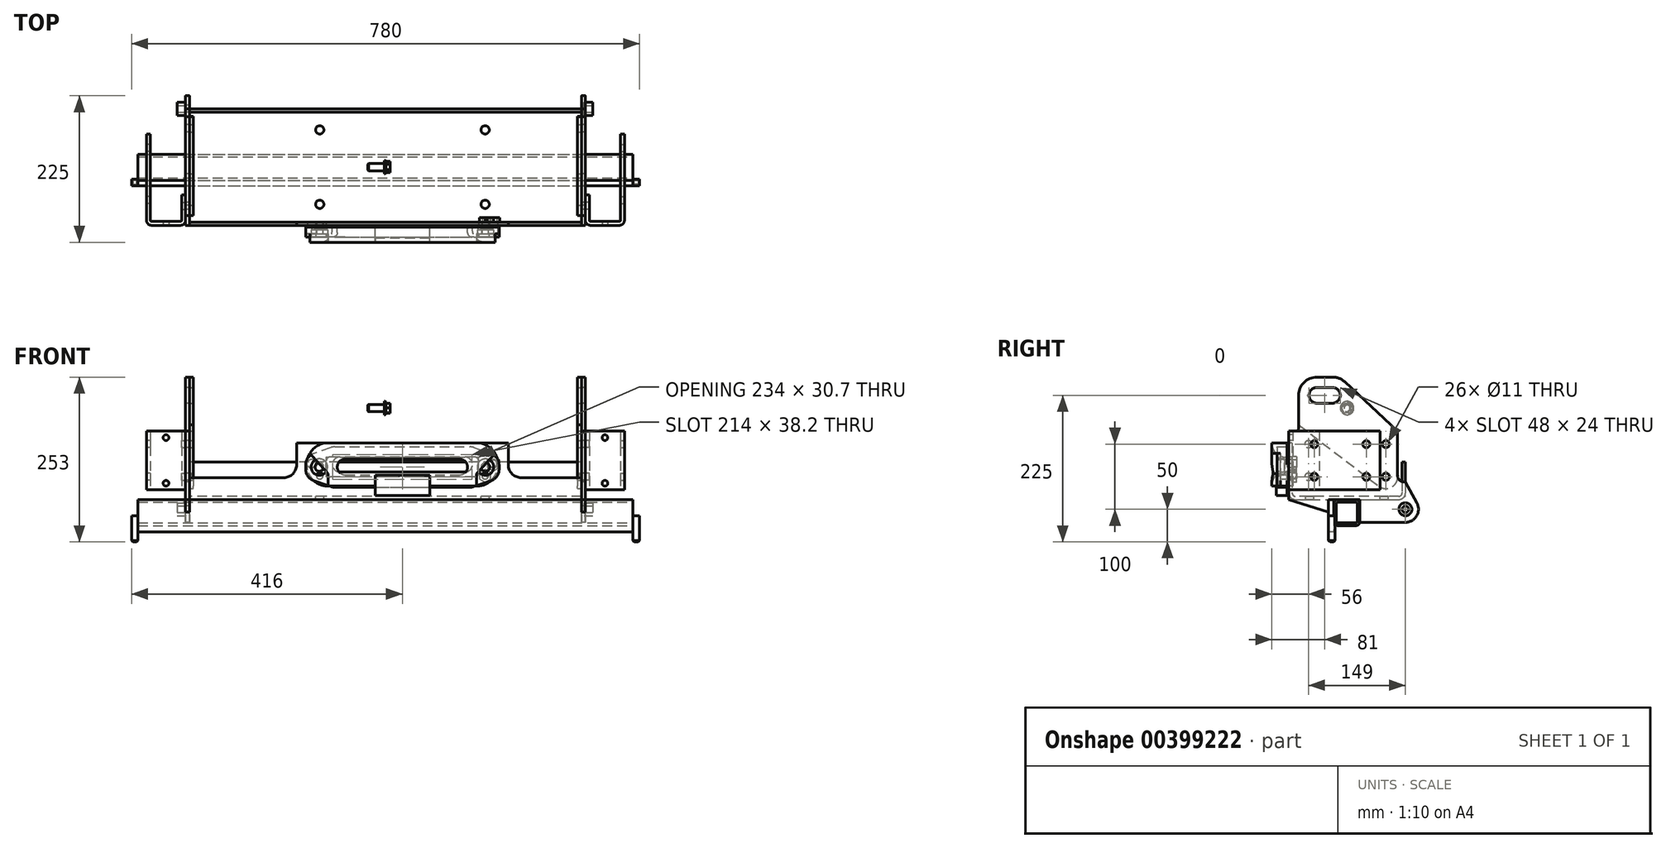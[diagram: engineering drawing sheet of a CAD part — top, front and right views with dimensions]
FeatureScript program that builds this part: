
annotation { "Feature Type Name" : "Feature", "Feature Type Description" : "" }
export const myFeature = defineFeature(function(context is Context, id is Id, definition is map)
    precondition{}
    {
        {
            var Q0;
            Q0=qCreatedBy(makeId("Right.planeOp"),FACE);
            var sketch = newSketch(context, id + "F0", { "sketchPlane" : qUnion([Q0])});
            skLineSegment(sketch, "E0", {"start": v(-84.5, 0) * mm, "end": v(84.5, 0) * mm});
            skLineSegment(sketch, "E1", {"start": v(-84.5, 0) * mm, "end": v(-84.5, 81.8) * mm});
            skLineSegment(sketch, "E2", {"start": v(84.5, 0) * mm, "end": v(84.5, 52.5) * mm});
            skLineSegment(sketch, "E3.0", {"start": v(-89.5, -5) * mm, "end": v(-89.5, 81.8) * mm});
            skLineSegment(sketch, "E3.1", {"start": v(-89.5, -5) * mm, "end": v(89.5, -5) * mm});
            skLineSegment(sketch, "E3.2", {"start": v(89.5, -5) * mm, "end": v(89.5, 52.5) * mm});
            skLineSegment(sketch, "E4", {"start": v(-89.5, 81.8) * mm, "end": v(-84.5, 81.8) * mm});
            skLineSegment(sketch, "E5", {"start": v(84.5, 52.5) * mm, "end": v(89.5, 52.5) * mm});
            skSolve(sketch);
        }
        {
            var Q0;
            Q0=qSketchRegion(id+"F0",true);
            extrude(context, id + "F1", {"entities" : qUnion([Q0]), "endBound" : BoundingType.SYMMETRIC, "depth" : 896 * mm});
        }
        {
            var Q0;
            Q0=makeQuery(id+"F1.opExtrude","SWEPT_FACE",FACE,{"disambiguationData":[OSD([sQuery(id+"F0.wireOp",EDGE,"E3.0")])]});
            var sketch = newSketch(context, id + "F2", { "sketchPlane" : qUnion([Q0])});
            skLineSegment(sketch, "E6", {"start": v(-448, 28.5) * mm, "end": v(-162.5, 28.5) * mm});
            skLineSegment(sketch, "E7", {"start": v(-162.5, 28.5) * mm, "end": v(-162.5, 81.8) * mm});
            skLineSegment(sketch, "E8", {"start": v(-162.5, 81.8) * mm, "end": v(162.5, 81.8) * mm});
            skLineSegment(sketch, "E9", {"start": v(162.5, 81.8) * mm, "end": v(162.5, 28.5) * mm});
            skLineSegment(sketch, "E10", {"start": v(162.5, 28.5) * mm, "end": v(448, 28.5) * mm});
            skLineSegment(sketch, "E11.bottom", {"start": v(-117, 60.2) * mm, "end": v(117, 60.2) * mm});
            skLineSegment(sketch, "E11.top", {"start": v(-117, 29.5) * mm, "end": v(117, 29.5) * mm});
            skLineSegment(sketch, "E11.left", {"start": v(-117, 60.2) * mm, "end": v(-117, 29.5) * mm});
            skLineSegment(sketch, "E11.right", {"start": v(117, 60.2) * mm, "end": v(117, 29.5) * mm});
            skCircle(sketch, "E12", {"center": v(-139.7, 50.1) * mm, "radius": 6.35 * mm});
            skCircle(sketch, "E13", {"center": v(139.7, 50.1) * mm, "radius": 6.35 * mm});
            skCircle(sketch, "E14", {"center": v(-127, 31.5) * mm, "radius": 5.1 * mm});
            skCircle(sketch, "E15", {"center": v(127, 31.5) * mm, "radius": 5.1 * mm});
            skLineSegment(sketch, "E16", {"start": v(-139.7, 50.1) * mm, "end": v(139.7, 50.1) * mm, "construction": true});
            skLineSegment(sketch, "E17", {"start": v(0, 60.2) * mm, "end": v(0, 29.5) * mm, "construction": true});
            skCircle(sketch, "E18", {"center": v(-127.5, 44.85) * mm, "radius": 5.1 * mm});
            skCircle(sketch, "E19.MirrorC", {"center": v(127.5, 44.85) * mm, "radius": 5.1 * mm});
            skLineSegment(sketch, "E20", {"start": v(-117, 44.85) * mm, "end": v(117, 44.85) * mm, "construction": true});
            skLineSegment(sketch, "E21", {"start": v(-117, 44.85) * mm, "end": v(-162.5, 44.85) * mm, "construction": true});
            skCircle(sketch, "E22", {"center": v(-127.5, 44.85) * mm, "radius": 6 * mm, "construction": true});
            skCircle(sketch, "E23", {"center": v(-139.7, 50.1) * mm, "radius": 6 * mm, "construction": true});
            skLineSegment(sketch, "E24", {"start": v(-127.5, 44.85) * mm, "end": v(-127.5, 24.22) * mm, "construction": true});
            skSolve(sketch);
        }
        {
            var Q0;
            Q0=qSketchRegion(id+"F2",true);
            var Q1;
            {var subQ0=sQuery(id+"F2.wireOp",EDGE,"E6");Q1=makeQuery(id+"F2.imprint","IMPRINT",FACE,{"disambiguationData":[TD([[makeQuery(id+"F2.imprint","IMPRINT",EDGE,{"derivedFrom":subQ0}),1.0]])]});}
            var Q2;
            {var subQ0=sQuery(id+"F2.wireOp",EDGE,"E9");Q2=makeQuery(id+"F2.imprint","IMPRINT",FACE,{"disambiguationData":[TD([[makeQuery(id+"F2.imprint","IMPRINT",EDGE,{"derivedFrom":subQ0}),1.0]])]});}
            extrude(context, id + "F3", {"entities" : qUnion([Q0, Q1, Q2]), "operationType" : NewBodyOperationType.REMOVE, "endBound" : BoundingType.UP_TO_NEXT, "oppositeDirection" : true, "depth" : 25 * mm});
        }
        {
            var Q0;
            Q0=makeQuery(id+"F1.opExtrude","SWEPT_FACE",FACE,{"disambiguationData":[OSD([sQuery(id+"F0.wireOp",EDGE,"E0")])]});
            var sketch = newSketch(context, id + "F4", { "sketchPlane" : qUnion([Q0])});
            skLineSegment(sketch, "E25.bottom", {"start": v(-127, 57.15) * mm, "end": v(127, 57.15) * mm, "construction": true});
            skLineSegment(sketch, "E25.top", {"start": v(-127, -57.15) * mm, "end": v(127, -57.15) * mm, "construction": true});
            skLineSegment(sketch, "E25.left", {"start": v(-127, 57.15) * mm, "end": v(-127, -57.15) * mm, "construction": true});
            skLineSegment(sketch, "E25.right", {"start": v(127, 57.15) * mm, "end": v(127, -57.15) * mm, "construction": true});
            skCircle(sketch, "E26", {"center": v(-127, 57.15) * mm, "radius": 6.35 * mm});
            skCircle(sketch, "E27", {"center": v(-127, -57.15) * mm, "radius": 6.35 * mm});
            skCircle(sketch, "E28", {"center": v(127, 57.15) * mm, "radius": 6.35 * mm});
            skCircle(sketch, "E29", {"center": v(127, -57.15) * mm, "radius": 6.35 * mm});
            skSolve(sketch);
        }
        {
            var Q0;
            Q0=qSketchRegion(id+"F4",true);
            extrude(context, id + "F5", {"entities" : qUnion([Q0]), "operationType" : NewBodyOperationType.REMOVE, "endBound" : BoundingType.UP_TO_NEXT, "oppositeDirection" : true, "depth" : 25 * mm});
        }
        {
            var Q0;
            Q0=makeQuery(id+"F3.boolean.opBoolean","COPY",EDGE,{"derivedFrom":makeQuery(id+"F3.opExtrude","SWEPT_EDGE",EDGE,{"disambiguationData":[OSD([sQuery(id+"F2.wireOp",EDGE,"E6"),sQuery(id+"F2.wireOp",EDGE,"E7")])]})});
            var Q1;
            Q1=makeQuery(id+"F3.boolean.opBoolean","COPY",EDGE,{"derivedFrom":makeQuery(id+"F3.opExtrude","SWEPT_EDGE",EDGE,{"disambiguationData":[OSD([sQuery(id+"F0.wireOp",EDGE,"E3.0"),sQuery(id+"F0.wireOp",EDGE,"E4"),sQuery(id+"F2.wireOp",EDGE,"E7"),sQuery(id+"F2.wireOp",EDGE,"E8")])]})});
            var Q2;
            Q2=makeQuery(id+"F3.boolean.opBoolean","COPY",EDGE,{"derivedFrom":makeQuery(id+"F3.opExtrude","SWEPT_EDGE",EDGE,{"disambiguationData":[OSD([sQuery(id+"F0.wireOp",EDGE,"E3.0"),sQuery(id+"F0.wireOp",EDGE,"E4"),sQuery(id+"F2.wireOp",EDGE,"E8"),sQuery(id+"F2.wireOp",EDGE,"E9")])]})});
            var Q3;
            Q3=makeQuery(id+"F3.boolean.opBoolean","COPY",EDGE,{"derivedFrom":makeQuery(id+"F3.opExtrude","SWEPT_EDGE",EDGE,{"disambiguationData":[OSD([sQuery(id+"F2.wireOp",EDGE,"E9"),sQuery(id+"F2.wireOp",EDGE,"E10")])]})});
            fillet(context, id + "F6", {"entities" : qUnion([Q0, Q1, Q2, Q3]), "radius" : 20 * mm, "tangentPropagation" : true, "allowEdgeOverflow" : false});
        }
        {
            var Q0;
            Q0=makeQuery(id+"F3.boolean.opBoolean","COPY",EDGE,{"derivedFrom":makeQuery(id+"F3.opExtrude","SWEPT_EDGE",EDGE,{"disambiguationData":[OSD([sQuery(id+"F2.wireOp",EDGE,"E11.top"),sQuery(id+"F2.wireOp",EDGE,"E11.right")])]})});
            var Q1;
            Q1=makeQuery(id+"F3.boolean.opBoolean","COPY",EDGE,{"derivedFrom":makeQuery(id+"F3.opExtrude","SWEPT_EDGE",EDGE,{"disambiguationData":[OSD([sQuery(id+"F2.wireOp",EDGE,"E11.bottom"),sQuery(id+"F2.wireOp",EDGE,"E11.right")])]})});
            var Q2;
            Q2=makeQuery(id+"F3.boolean.opBoolean","COPY",EDGE,{"derivedFrom":makeQuery(id+"F3.opExtrude","SWEPT_EDGE",EDGE,{"disambiguationData":[OSD([sQuery(id+"F2.wireOp",EDGE,"E11.top"),sQuery(id+"F2.wireOp",EDGE,"E11.left")])]})});
            var Q3;
            Q3=makeQuery(id+"F3.boolean.opBoolean","COPY",EDGE,{"derivedFrom":makeQuery(id+"F3.opExtrude","SWEPT_EDGE",EDGE,{"disambiguationData":[OSD([sQuery(id+"F2.wireOp",EDGE,"E11.bottom"),sQuery(id+"F2.wireOp",EDGE,"E11.left")])]})});
            fillet(context, id + "F7", {"entities" : qUnion([Q0, Q1, Q2, Q3]), "radius" : 6 * mm, "allowEdgeOverflow" : false});
        }
        {
            var Q0;
            Q0=makeQuery(id+"F1.opExtrude","SWEPT_EDGE",EDGE,{"disambiguationData":[OSD([sQuery(id+"F0.wireOp",EDGE,"E0"),sQuery(id+"F0.wireOp",EDGE,"E2")])]});
            var Q1;
            Q1=makeQuery(id+"F1.opExtrude","SWEPT_EDGE",EDGE,{"disambiguationData":[OSD([sQuery(id+"F0.wireOp",EDGE,"E0"),sQuery(id+"F0.wireOp",EDGE,"E1")])]});
            fillet(context, id + "F8", {"entities" : qUnion([Q0, Q1]), "radius" : 5 * mm, "allowEdgeOverflow" : false});
        }
        {
            var Q0;
            Q0=makeQuery(id+"F1.opExtrude","SWEPT_EDGE",EDGE,{"disambiguationData":[OSD([sQuery(id+"F0.wireOp",EDGE,"E3.1"),sQuery(id+"F0.wireOp",EDGE,"E3.2")])]});
            var Q1;
            Q1=makeQuery(id+"F1.opExtrude","SWEPT_EDGE",EDGE,{"disambiguationData":[OSD([sQuery(id+"F0.wireOp",EDGE,"E3.0"),sQuery(id+"F0.wireOp",EDGE,"E3.1")])]});
            fillet(context, id + "F9", {"entities" : qUnion([Q0, Q1]), "radius" : 10 * mm, "allowEdgeOverflow" : false});
        }
        {
            var Q0;
            Q0=makeQuery(id+"F1.opExtrude","SWEPT_FACE",FACE,{"disambiguationData":[OSD([sQuery(id+"F0.wireOp",EDGE,"E3.0")])]});
            var sketch = newSketch(context, id + "F10", { "sketchPlane" : qUnion([Q0])});
            skCircle(sketch, "E30.0", {"center": v(-127, 31.5) * mm, "radius": 5.1 * mm});
            skCircle(sketch, "E31.0", {"center": v(127, 31.5) * mm, "radius": 5.1 * mm});
            skArc(sketch, "E32", {"start": v(-113.7, 82.1) * mm, "mid": v(-147, 48.8) * mm, "end": v(-113.7, 15.5) * mm});
            skArc(sketch, "E33", {"start": v(113.7, 15.5) * mm, "mid": v(147, 48.8) * mm, "end": v(113.7, 82.1) * mm});
            skLineSegment(sketch, "E34", {"start": v(-113.7, 82.1) * mm, "end": v(113.7, 82.1) * mm});
            skLineSegment(sketch, "E35", {"start": v(-113.7, 15.5) * mm, "end": v(-42, 15.5) * mm});
            skArc(sketch, "E36", {"start": v(-96, 60.3) * mm, "mid": v(-107.5, 48.8) * mm, "end": v(-96, 37.3) * mm});
            skArc(sketch, "E37", {"start": v(96, 37.3) * mm, "mid": v(107.5, 48.8) * mm, "end": v(96, 60.3) * mm});
            skLineSegment(sketch, "E38", {"start": v(-96, 60.3) * mm, "end": v(96, 60.3) * mm});
            skLineSegment(sketch, "E39", {"start": v(-96, 37.3) * mm, "end": v(96, 37.3) * mm});
            skLineSegment(sketch, "E40.top", {"start": v(-42, 1.1) * mm, "end": v(42, 1.1) * mm});
            skLineSegment(sketch, "E40.left", {"start": v(-42, 15.5) * mm, "end": v(-42, 1.1) * mm});
            skLineSegment(sketch, "E40.right", {"start": v(42, 15.5) * mm, "end": v(42, 1.1) * mm});
            skLineSegment(sketch, "E41.trimOffspring", {"start": v(42, 15.5) * mm, "end": v(113.7, 15.5) * mm});
            skSolve(sketch);
        }
        {
            var Q0;
            Q0=qSketchRegion(id+"F10",true);
            extrude(context, id + "F11", {"entities" : qUnion([Q0]), "depth" : 23 * mm});
        }
        {
            var Q0;
            Q0=makeQuery(id+"F11.opExtrude","SWEPT_BODY",BODY,{"disambiguationData":[OSD([sQuery(id+"F10.wireOp",EDGE,"E30.0"),sQuery(id+"F10.wireOp",EDGE,"E31.0"),sQuery(id+"F10.wireOp",EDGE,"E32"),sQuery(id+"F10.wireOp",EDGE,"E33"),sQuery(id+"F10.wireOp",EDGE,"E34"),sQuery(id+"F10.wireOp",EDGE,"E35"),sQuery(id+"F10.wireOp",EDGE,"E36"),sQuery(id+"F10.wireOp",EDGE,"E37"),sQuery(id+"F10.wireOp",EDGE,"E38"),sQuery(id+"F10.wireOp",EDGE,"E39"),sQuery(id+"F10.wireOp",EDGE,"E40.top"),sQuery(id+"F10.wireOp",EDGE,"E40.left"),sQuery(id+"F10.wireOp",EDGE,"E40.right"),sQuery(id+"F10.wireOp",EDGE,"E41.trimOffspring")])]});
            transform(context, id + "F12", {"entities" : qUnion([Q0]), "transformType" : TransformType.TRANSLATION_3D, "dx" : 0 * mm, "dy" : -3 * mm, "dz" : 0 * mm, "makeCopy" : false});
        }
        {
            var Q0;
            Q0=makeQuery(id+"F11.opExtrude","CAP_EDGE",EDGE,{"disambiguationData":[OSD([sQuery(id+"F10.wireOp",EDGE,"E37")])],"isStart":false});
            fillet(context, id + "F13", {"entities" : qUnion([Q0]), "radius" : 20 * mm, "tangentPropagation" : true, "allowEdgeOverflow" : false});
        }
        {
            var Q0;
            Q0=makeQuery(id+"F11.opExtrude","CAP_FACE",FACE,{"disambiguationData":[OSD([sQuery(id+"F10.wireOp",EDGE,"E30.0"),sQuery(id+"F10.wireOp",EDGE,"E31.0"),sQuery(id+"F10.wireOp",EDGE,"E32"),sQuery(id+"F10.wireOp",EDGE,"E33"),sQuery(id+"F10.wireOp",EDGE,"E34"),sQuery(id+"F10.wireOp",EDGE,"E35"),sQuery(id+"F10.wireOp",EDGE,"E36"),sQuery(id+"F10.wireOp",EDGE,"E37"),sQuery(id+"F10.wireOp",EDGE,"E38"),sQuery(id+"F10.wireOp",EDGE,"E39"),sQuery(id+"F10.wireOp",EDGE,"E40.top"),sQuery(id+"F10.wireOp",EDGE,"E40.left"),sQuery(id+"F10.wireOp",EDGE,"E40.right"),sQuery(id+"F10.wireOp",EDGE,"E41.trimOffspring")])],"isStart":false});
            var sketch = newSketch(context, id + "F14", { "sketchPlane" : qUnion([Q0])});
            skLineSegment(sketch, "E42.bottom", {"start": v(-42, 1.1) * mm, "end": v(42, 1.1) * mm});
            skLineSegment(sketch, "E42.top", {"start": v(-42, 40.98) * mm, "end": v(42, 40.98) * mm});
            skLineSegment(sketch, "E42.left", {"start": v(-42, 1.1) * mm, "end": v(-42, 40.98) * mm});
            skLineSegment(sketch, "E42.right", {"start": v(42, 1.1) * mm, "end": v(42, 40.98) * mm});
            skSolve(sketch);
        }
        {
            var Q0;
            Q0=qSketchRegion(id+"F14",true);
            extrude(context, id + "F15", {"entities" : qUnion([Q0]), "operationType" : NewBodyOperationType.REMOVE, "oppositeDirection" : true, "depth" : 6.5 * mm});
        }
        {
            var Q0;
            Q0=makeQuery(id+"F11.opExtrude","CAP_FACE",FACE,{"disambiguationData":[OSD([sQuery(id+"F10.wireOp",EDGE,"E30.0"),sQuery(id+"F10.wireOp",EDGE,"E31.0"),sQuery(id+"F10.wireOp",EDGE,"E32"),sQuery(id+"F10.wireOp",EDGE,"E33"),sQuery(id+"F10.wireOp",EDGE,"E34"),sQuery(id+"F10.wireOp",EDGE,"E35"),sQuery(id+"F10.wireOp",EDGE,"E36"),sQuery(id+"F10.wireOp",EDGE,"E37"),sQuery(id+"F10.wireOp",EDGE,"E38"),sQuery(id+"F10.wireOp",EDGE,"E39"),sQuery(id+"F10.wireOp",EDGE,"E40.top"),sQuery(id+"F10.wireOp",EDGE,"E40.left"),sQuery(id+"F10.wireOp",EDGE,"E40.right"),sQuery(id+"F10.wireOp",EDGE,"E41.trimOffspring")])],"isStart":false});
            var sketch = newSketch(context, id + "F16", { "sketchPlane" : qUnion([Q0])});
            skArc(sketch, "E43.0", {"start": v(-142.15, 66.1) * mm, "mid": v(-142.8, 32.6) * mm, "end": v(-114, 15.5) * mm});
            skLineSegment(sketch, "E44", {"start": v(-142.15, 66.1) * mm, "end": v(-114, 34.5) * mm});
            skLineSegment(sketch, "E45", {"start": v(-114, 34.5) * mm, "end": v(-114, 15.5) * mm});
            skLineSegment(sketch, "E46", {"start": v(0, -35.84) * mm, "end": v(0, 92.87) * mm, "construction": true});
            skLineSegment(sketch, "E47.MirrorCS", {"start": v(142.15, 66.1) * mm, "end": v(114, 34.5) * mm});
            skArc(sketch, "E48.MirrorCS", {"start": v(142.15, 66.1) * mm, "mid": v(142.8, 32.6) * mm, "end": v(114, 15.5) * mm});
            skLineSegment(sketch, "E49.MirrorCS", {"start": v(114, 34.5) * mm, "end": v(114, 15.5) * mm});
            skSolve(sketch);
        }
        {
            var Q0;
            Q0=qSketchRegion(id+"F16",true);
            extrude(context, id + "F17", {"entities" : qUnion([Q0]), "operationType" : NewBodyOperationType.REMOVE, "oppositeDirection" : true, "depth" : 13 * mm});
        }
        {
            var Q0;
            Q0=makeQuery(id+"F1.opExtrude","SWEPT_FACE",FACE,{"disambiguationData":[OSD([sQuery(id+"F0.wireOp",EDGE,"E3.1")])]});
            var sketch = newSketch(context, id + "F18", { "sketchPlane" : qUnion([Q0])});
            skLineSegment(sketch, "E50.bottom", {"start": v(448, 89.58) * mm, "end": v(275, 89.58) * mm});
            skLineSegment(sketch, "E50.top", {"start": v(448, -89.63) * mm, "end": v(275, -89.63) * mm});
            skLineSegment(sketch, "E50.left", {"start": v(448, 89.58) * mm, "end": v(448, -89.63) * mm});
            skLineSegment(sketch, "E50.right", {"start": v(275, 89.58) * mm, "end": v(275, -89.63) * mm});
            skLineSegment(sketch, "E51.bottom", {"start": v(-448, 89.51) * mm, "end": v(-327, 89.51) * mm});
            skLineSegment(sketch, "E51.top", {"start": v(-448, -89.5) * mm, "end": v(-327, -89.5) * mm});
            skLineSegment(sketch, "E51.left", {"start": v(-448, 89.51) * mm, "end": v(-448, -89.5) * mm});
            skLineSegment(sketch, "E51.right", {"start": v(-327, 89.51) * mm, "end": v(-327, -89.5) * mm});
            skSolve(sketch);
        }
        {
            var Q0;
            Q0=qSketchRegion(id+"F18",true);
            extrude(context, id + "F19", {"entities" : qUnion([Q0]), "operationType" : NewBodyOperationType.REMOVE, "endBound" : BoundingType.THROUGH_ALL, "oppositeDirection" : true, "depth" : 25 * mm});
        }
        {
            var Q0;
            Q0=makeQuery(id+"F19.boolean.opBoolean","COPY",FACE,{"derivedFrom":makeQuery(id+"F19.opExtrude","SWEPT_FACE",FACE,{"disambiguationData":[OSD([sQuery(id+"F18.wireOp",EDGE,"E50.right")])]})});
            var sketch = newSketch(context, id + "F20", { "sketchPlane" : qUnion([Q0])});
            skCircle(sketch, "E52", {"center": v(89.5, -20) * mm, "radius": 5.5 * mm});
            skCircle(sketch, "E53", {"center": v(59.5, 30) * mm, "radius": 5.5 * mm});
            skCircle(sketch, "E54", {"center": v(59.5, 80) * mm, "radius": 5.5 * mm});
            skLineSegment(sketch, "E55", {"start": v(-89.5, 100) * mm, "end": v(-89.5, -5) * mm});
            skLineSegment(sketch, "E56", {"start": v(-28.7, -24.52) * mm, "end": v(-28.7, -5) * mm});
            skLineSegment(sketch, "E57", {"start": v(-28.7, -5) * mm, "end": v(19.5, -5) * mm});
            skLineSegment(sketch, "E58", {"start": v(19.5, -5) * mm, "end": v(19.5, -40) * mm});
            skLineSegment(sketch, "E59", {"start": v(19.5, -40) * mm, "end": v(89.5, -40) * mm});
            skArc(sketch, "E60", {"start": v(89.5, -40) * mm, "mid": v(106.68, -30.24) * mm, "end": v(107.09, -10.48) * mm});
            skLineSegment(sketch, "E61", {"start": v(89.5, 22) * mm, "end": v(107.09, -10.48) * mm});
            skLineSegment(sketch, "E62", {"start": v(89.5, 22) * mm, "end": v(87.5, 22) * mm});
            skLineSegment(sketch, "E63", {"start": v(77.5, 32) * mm, "end": v(77.5, 100) * mm});
            skLineSegment(sketch, "E64", {"start": v(-22.5, 183) * mm, "end": v(-46.5, 183) * mm});
            skLineSegment(sketch, "E65", {"start": v(-79.5, 100) * mm, "end": v(-89.5, 100) * mm});
            skCircle(sketch, "E66", {"center": v(-46.5, 155) * mm, "radius": 12 * mm});
            skCircle(sketch, "E67", {"center": v(-22.5, 155) * mm, "radius": 12 * mm});
            skLineSegment(sketch, "E68", {"start": v(-46.5, 167) * mm, "end": v(-22.5, 167) * mm});
            skLineSegment(sketch, "E69", {"start": v(-46.5, 143) * mm, "end": v(-22.5, 143) * mm});
            skPoint(sketch, "E70.visualSharp", {"position": v(-45.45, 100) * mm});
            skArc(sketch, "E70.filletArc", {"start": v(-79.5, 100) * mm, "mid": v(-75.96, 101.46) * mm, "end": v(-74.5, 105) * mm});
            skPoint(sketch, "E71.visualSharp", {"position": v(77.5, 22) * mm});
            skArc(sketch, "E71.filletArc", {"start": v(77.5, 32) * mm, "mid": v(80.43, 24.93) * mm, "end": v(87.5, 22) * mm});
            skArc(sketch, "E72", {"start": v(-3.4, 175.47) * mm, "mid": v(-12.24, 181.05) * mm, "end": v(-22.5, 183) * mm});
            skArc(sketch, "E73", {"start": v(-46.5, 183) * mm, "mid": v(-66.3, 174.8) * mm, "end": v(-74.5, 155) * mm});
            skLineSegment(sketch, "E74", {"start": v(-89.5, -5) * mm, "end": v(19.5, -40) * mm, "construction": true});
            skLineSegment(sketch, "E75", {"start": v(-89.5, -5) * mm, "end": v(-28.7, -24.52) * mm});
            skLineSegment(sketch, "E76", {"start": v(-79.5, 100) * mm, "end": v(77.5, 100) * mm, "construction": true});
            skLineSegment(sketch, "E77", {"start": v(77.5, 100) * mm, "end": v(-3.4, 175.47) * mm});
            skLineSegment(sketch, "E78", {"start": v(-74.5, 105) * mm, "end": v(-74.5, 155) * mm});
            skSolve(sketch);
        }
        {
            var Q0;
            Q0=qSketchRegion(id+"F20",true);
            extrude(context, id + "F21", {"entities" : qUnion([Q0]), "depth" : 6 * mm});
        }
        {
            var Q0;
            Q0=makeQuery(id+"F21.opExtrude","SWEPT_BODY",BODY,{"disambiguationData":[OSD([sQuery(id+"F20.wireOp",EDGE,"E52"),sQuery(id+"F20.wireOp",EDGE,"E53"),sQuery(id+"F20.wireOp",EDGE,"E54"),sQuery(id+"F20.wireOp",EDGE,"E55"),sQuery(id+"F20.wireOp",EDGE,"XvVVhRg5-2krd-yFCo-rq4G-s1C9oEQ6HOLZ"),sQuery(id+"F20.wireOp",EDGE,"E56"),sQuery(id+"F20.wireOp",EDGE,"E57"),sQuery(id+"F20.wireOp",EDGE,"E58"),sQuery(id+"F20.wireOp",EDGE,"E59"),sQuery(id+"F20.wireOp",EDGE,"E60"),sQuery(id+"F20.wireOp",EDGE,"E61"),sQuery(id+"F20.wireOp",EDGE,"E62"),sQuery(id+"F20.wireOp",EDGE,"E63"),sQuery(id+"F20.wireOp",EDGE,"E64"),sQuery(id+"F20.wireOp",EDGE,"lX6jeAK8-40P4-eBXy-fJTd-rd2ZCsxYktxP"),sQuery(id+"F20.wireOp",EDGE,"E65"),sQuery(id+"F20.wireOp",EDGE,"E66"),sQuery(id+"F20.wireOp",EDGE,"E67"),sQuery(id+"F20.wireOp",EDGE,"E68"),sQuery(id+"F20.wireOp",EDGE,"E69")])]});
            var Q1;
            {var subQ0=sQuery(id+"F0.wireOp",EDGE,"E0");Q1=makeQuery(id+"F8.opFillet","BLEND_EDGE",EDGE,{"blendedFrom":[makeQuery(id+"F1.opExtrude","SWEPT_EDGE",EDGE,{"disambiguationData":[OSD([subQ0,sQuery(id+"F0.wireOp",EDGE,"E2")])]}),makeQuery(id+"F1.opExtrude","SWEPT_FACE",FACE,{"disambiguationData":[OSD([subQ0])]})],"blendedInto":[makeQuery(id+"F1.opExtrude","SWEPT_FACE",FACE,{"disambiguationData":[OSD([subQ0])]})]});}
            var Q2;
            {var subQ0=sQuery(id+"F0.wireOp",EDGE,"E0");Q2=makeQuery(id+"F8.opFillet","BLEND_EDGE",EDGE,{"blendedFrom":[makeQuery(id+"F1.opExtrude","SWEPT_EDGE",EDGE,{"disambiguationData":[OSD([subQ0,sQuery(id+"F0.wireOp",EDGE,"E2")])]}),makeQuery(id+"F1.opExtrude","SWEPT_FACE",FACE,{"disambiguationData":[OSD([subQ0])]})],"blendedInto":[makeQuery(id+"F1.opExtrude","SWEPT_FACE",FACE,{"disambiguationData":[OSD([subQ0])]})]});}
            transform(context, id + "F22", {"entities" : qUnion([Q0]), "transformType" : TransformType.TRANSLATION_DISTANCE, "transformDirection" : qUnion([Q2]), "distance" : 608 * mm, "makeCopy" : true});
        }
        {
            var Q0;
            Q0=makeQuery(id+"F21.opExtrude","CAP_FACE",FACE,{"disambiguationData":[OSD([sQuery(id+"F20.wireOp",EDGE,"E52"),sQuery(id+"F20.wireOp",EDGE,"E53"),sQuery(id+"F20.wireOp",EDGE,"E54"),sQuery(id+"F20.wireOp",EDGE,"E55"),sQuery(id+"F20.wireOp",EDGE,"E56"),sQuery(id+"F20.wireOp",EDGE,"E57"),sQuery(id+"F20.wireOp",EDGE,"E58"),sQuery(id+"F20.wireOp",EDGE,"E59"),sQuery(id+"F20.wireOp",EDGE,"E60"),sQuery(id+"F20.wireOp",EDGE,"E61"),sQuery(id+"F20.wireOp",EDGE,"E62"),sQuery(id+"F20.wireOp",EDGE,"E63"),sQuery(id+"F20.wireOp",EDGE,"E64"),sQuery(id+"F20.wireOp",EDGE,"E65"),sQuery(id+"F20.wireOp",EDGE,"E66"),sQuery(id+"F20.wireOp",EDGE,"E67"),sQuery(id+"F20.wireOp",EDGE,"E68"),sQuery(id+"F20.wireOp",EDGE,"E69"),sQuery(id+"F20.wireOp",EDGE,"E70.filletArc"),sQuery(id+"F20.wireOp",EDGE,"E71.filletArc"),sQuery(id+"F20.wireOp",EDGE,"E72"),sQuery(id+"F20.wireOp",EDGE,"E73"),sQuery(id+"F20.wireOp",EDGE,"E75"),sQuery(id+"F20.wireOp",EDGE,"E77"),sQuery(id+"F20.wireOp",EDGE,"E78")])],"isStart":true});
            var sketch = newSketch(context, id + "F23", { "sketchPlane" : qUnion([Q0])});
            skCircle(sketch, "E79.0", {"center": v(-59.5, 30) * mm, "radius": 5.5 * mm});
            skCircle(sketch, "E80.0", {"center": v(-59.5, 80) * mm, "radius": 5.5 * mm});
            skLineSegment(sketch, "E81.0", {"start": v(-77.5, 100) * mm, "end": v(3.4, 175.47) * mm});
            skArc(sketch, "E82.0", {"start": v(3.4, 175.47) * mm, "mid": v(12.24, 181.05) * mm, "end": v(22.5, 183) * mm});
            skLineSegment(sketch, "E83.0", {"start": v(22.5, 183) * mm, "end": v(46.5, 183) * mm});
            skArc(sketch, "E84.0", {"start": v(46.5, 183) * mm, "mid": v(66.3, 174.8) * mm, "end": v(74.5, 155) * mm});
            skArc(sketch, "E85.0", {"start": v(46.5, 167) * mm, "mid": v(58.5, 155) * mm, "end": v(46.5, 143) * mm});
            skLineSegment(sketch, "E86.0", {"start": v(46.5, 167) * mm, "end": v(22.5, 167) * mm});
            skArc(sketch, "E87.0", {"start": v(22.5, 143) * mm, "mid": v(10.5, 155) * mm, "end": v(22.5, 167) * mm});
            skLineSegment(sketch, "E88.0", {"start": v(46.5, 143) * mm, "end": v(22.5, 143) * mm});
            skCircle(sketch, "E89", {"center": v(-59.5, 30) * mm, "radius": 18.21 * mm});
            skLineSegment(sketch, "E90", {"start": v(-77.5, 100) * mm, "end": v(-77.5, 27.23) * mm});
            skLineSegment(sketch, "E91", {"start": v(74.5, 155) * mm, "end": v(74.5, 110) * mm});
            skLineSegment(sketch, "E92", {"start": v(74.5, 110) * mm, "end": v(-48.4, 15.56) * mm});
            skSolve(sketch);
        }
        {
            var Q0;
            Q0=qSketchRegion(id+"F23",true);
            extrude(context, id + "F24", {"entities" : qUnion([Q0]), "depth" : 6 * mm});
        }
        {
            var Q0;
            Q0=makeQuery(id+"F24.opExtrude","SWEPT_BODY",BODY,{"disambiguationData":[OSD([sQuery(id+"F23.wireOp",EDGE,"E79.0"),sQuery(id+"F23.wireOp",EDGE,"E80.0"),sQuery(id+"F23.wireOp",EDGE,"E81.0"),sQuery(id+"F23.wireOp",EDGE,"E82.0"),sQuery(id+"F23.wireOp",EDGE,"E83.0"),sQuery(id+"F23.wireOp",EDGE,"E84.0"),sQuery(id+"F23.wireOp",EDGE,"E85.0"),sQuery(id+"F23.wireOp",EDGE,"E86.0"),sQuery(id+"F23.wireOp",EDGE,"E87.0"),sQuery(id+"F23.wireOp",EDGE,"E88.0"),sQuery(id+"F23.wireOp",EDGE,"E89"),sQuery(id+"F23.wireOp",EDGE,"E90"),sQuery(id+"F23.wireOp",EDGE,"E91"),sQuery(id+"F23.wireOp",EDGE,"E92")])]});
            var Q1;
            Q1=makeQuery(id+"F1.opExtrude","SWEPT_EDGE",EDGE,{"disambiguationData":[OSD([sQuery(id+"F0.wireOp",EDGE,"E2"),sQuery(id+"F0.wireOp",EDGE,"E5")])]});
            transform(context, id + "F25", {"entities" : qUnion([Q0]), "transformType" : TransformType.TRANSLATION_DISTANCE, "transformDirection" : qUnion([Q1]), "distance" : 596 * mm, "makeCopy" : true});
        }
        {
            var Q0;
            Q0=makeQuery(id+"F21.opExtrude","CAP_FACE",FACE,{"disambiguationData":[OSD([sQuery(id+"F20.wireOp",EDGE,"E52"),sQuery(id+"F20.wireOp",EDGE,"E53"),sQuery(id+"F20.wireOp",EDGE,"E54"),sQuery(id+"F20.wireOp",EDGE,"E55"),sQuery(id+"F20.wireOp",EDGE,"XvVVhRg5-2krd-yFCo-rq4G-s1C9oEQ6HOLZ"),sQuery(id+"F20.wireOp",EDGE,"E56"),sQuery(id+"F20.wireOp",EDGE,"E57"),sQuery(id+"F20.wireOp",EDGE,"E58"),sQuery(id+"F20.wireOp",EDGE,"E59"),sQuery(id+"F20.wireOp",EDGE,"E60"),sQuery(id+"F20.wireOp",EDGE,"E61"),sQuery(id+"F20.wireOp",EDGE,"E62"),sQuery(id+"F20.wireOp",EDGE,"E63"),sQuery(id+"F20.wireOp",EDGE,"E64"),sQuery(id+"F20.wireOp",EDGE,"lX6jeAK8-40P4-eBXy-fJTd-rd2ZCsxYktxP"),sQuery(id+"F20.wireOp",EDGE,"E65"),sQuery(id+"F20.wireOp",EDGE,"E66"),sQuery(id+"F20.wireOp",EDGE,"E67"),sQuery(id+"F20.wireOp",EDGE,"E68"),sQuery(id+"F20.wireOp",EDGE,"E69")])],"isStart":false});
            var sketch = newSketch(context, id + "F26", { "sketchPlane" : qUnion([Q0])});
            skLineSegment(sketch, "E93.bottom", {"start": v(-14.5, -5) * mm, "end": v(13.5, -5) * mm});
            skLineSegment(sketch, "E93.top", {"start": v(-14.5, -45) * mm, "end": v(13.5, -45) * mm});
            skLineSegment(sketch, "E93.left", {"start": v(-20.5, -11) * mm, "end": v(-20.5, -39) * mm});
            skLineSegment(sketch, "E93.right", {"start": v(19.5, -11) * mm, "end": v(19.5, -39) * mm});
            skPoint(sketch, "E94.visualSharp", {"position": v(-20.5, -5) * mm});
            skArc(sketch, "E94.filletArc", {"start": v(-14.5, -5) * mm, "mid": v(-18.74, -6.76) * mm, "end": v(-20.5, -11) * mm});
            skPoint(sketch, "E95.visualSharp", {"position": v(19.5, -5) * mm});
            skArc(sketch, "E95.filletArc", {"start": v(19.5, -11) * mm, "mid": v(17.74, -6.76) * mm, "end": v(13.5, -5) * mm});
            skPoint(sketch, "E96.visualSharp", {"position": v(19.5, -45) * mm});
            skArc(sketch, "E96.filletArc", {"start": v(13.5, -45) * mm, "mid": v(17.74, -43.24) * mm, "end": v(19.5, -39) * mm});
            skPoint(sketch, "E97.visualSharp", {"position": v(-20.5, -45) * mm});
            skArc(sketch, "E97.filletArc", {"start": v(-20.5, -39) * mm, "mid": v(-18.74, -43.24) * mm, "end": v(-14.5, -45) * mm});
            skLineSegment(sketch, "E98.0", {"start": v(-14.5, -9) * mm, "end": v(13.5, -9) * mm});
            skArc(sketch, "E98.1", {"start": v(15.5, -11) * mm, "mid": v(14.91, -9.59) * mm, "end": v(13.5, -9) * mm});
            skArc(sketch, "E98.2", {"start": v(-14.5, -9) * mm, "mid": v(-15.91, -9.59) * mm, "end": v(-16.5, -11) * mm});
            skLineSegment(sketch, "E98.3", {"start": v(15.5, -11) * mm, "end": v(15.5, -39) * mm});
            skLineSegment(sketch, "E98.4", {"start": v(-16.5, -11) * mm, "end": v(-16.5, -39) * mm});
            skArc(sketch, "E98.5", {"start": v(-16.5, -39) * mm, "mid": v(-15.91, -40.41) * mm, "end": v(-14.5, -41) * mm});
            skLineSegment(sketch, "E98.6", {"start": v(-14.5, -41) * mm, "end": v(13.5, -41) * mm});
            skArc(sketch, "E98.7", {"start": v(13.5, -41) * mm, "mid": v(14.91, -40.41) * mm, "end": v(15.5, -39) * mm});
            skSolve(sketch);
        }
        {
            var Q0;
            Q0=qSketchRegion(id+"F26",true);
            extrude(context, id + "F27", {"entities" : qUnion([Q0]), "oppositeDirection" : true, "depth" : 687 * mm, "hasSecondDirection" : true, "secondDirectionOppositeDirection" : false, "secondDirectionDepth" : 73 * mm});
        }
        {
            var Q0;
            Q0=makeQuery(id+"F21.opExtrude","CAP_FACE",FACE,{"disambiguationData":[OSD([sQuery(id+"F20.wireOp",EDGE,"E52"),sQuery(id+"F20.wireOp",EDGE,"E53"),sQuery(id+"F20.wireOp",EDGE,"E54"),sQuery(id+"F20.wireOp",EDGE,"E55"),sQuery(id+"F20.wireOp",EDGE,"XvVVhRg5-2krd-yFCo-rq4G-s1C9oEQ6HOLZ"),sQuery(id+"F20.wireOp",EDGE,"E56"),sQuery(id+"F20.wireOp",EDGE,"E57"),sQuery(id+"F20.wireOp",EDGE,"E58"),sQuery(id+"F20.wireOp",EDGE,"E59"),sQuery(id+"F20.wireOp",EDGE,"E60"),sQuery(id+"F20.wireOp",EDGE,"E61"),sQuery(id+"F20.wireOp",EDGE,"E62"),sQuery(id+"F20.wireOp",EDGE,"E63"),sQuery(id+"F20.wireOp",EDGE,"E64"),sQuery(id+"F20.wireOp",EDGE,"lX6jeAK8-40P4-eBXy-fJTd-rd2ZCsxYktxP"),sQuery(id+"F20.wireOp",EDGE,"E65"),sQuery(id+"F20.wireOp",EDGE,"E66"),sQuery(id+"F20.wireOp",EDGE,"E67"),sQuery(id+"F20.wireOp",EDGE,"E68"),sQuery(id+"F20.wireOp",EDGE,"E69")])],"isStart":true});
            var sketch = newSketch(context, id + "F28", { "sketchPlane" : qUnion([Q0])});
            skLineSegment(sketch, "E99.bottom", {"start": v(20.5, -5) * mm, "end": v(28.5, -5) * mm});
            skLineSegment(sketch, "E99.top", {"start": v(20.5, -55) * mm, "end": v(28.5, -55) * mm});
            skLineSegment(sketch, "E99.left", {"start": v(20.5, -5) * mm, "end": v(20.5, -55) * mm});
            skLineSegment(sketch, "E99.right", {"start": v(28.5, -5) * mm, "end": v(28.5, -55) * mm});
            skSolve(sketch);
        }
        {
            var Q0;
            Q0=qSketchRegion(id+"F28",true);
            var Q1;
            Q1=makeQuery(id+"F22.opPattern","COPY",BODY,{"derivedFrom":makeQuery(id+"F21.opExtrude","SWEPT_BODY",BODY,{"disambiguationData":[OSD([sQuery(id+"F20.wireOp",EDGE,"E52"),sQuery(id+"F20.wireOp",EDGE,"E53"),sQuery(id+"F20.wireOp",EDGE,"E54"),sQuery(id+"F20.wireOp",EDGE,"E55"),sQuery(id+"F20.wireOp",EDGE,"XvVVhRg5-2krd-yFCo-rq4G-s1C9oEQ6HOLZ"),sQuery(id+"F20.wireOp",EDGE,"E56"),sQuery(id+"F20.wireOp",EDGE,"E57"),sQuery(id+"F20.wireOp",EDGE,"E58"),sQuery(id+"F20.wireOp",EDGE,"E59"),sQuery(id+"F20.wireOp",EDGE,"E60"),sQuery(id+"F20.wireOp",EDGE,"E61"),sQuery(id+"F20.wireOp",EDGE,"E62"),sQuery(id+"F20.wireOp",EDGE,"E63"),sQuery(id+"F20.wireOp",EDGE,"E64"),sQuery(id+"F20.wireOp",EDGE,"lX6jeAK8-40P4-eBXy-fJTd-rd2ZCsxYktxP"),sQuery(id+"F20.wireOp",EDGE,"E65"),sQuery(id+"F20.wireOp",EDGE,"E66"),sQuery(id+"F20.wireOp",EDGE,"E67"),sQuery(id+"F20.wireOp",EDGE,"E68"),sQuery(id+"F20.wireOp",EDGE,"E69")])]}),"instanceName":"1"});
            extrude(context, id + "F29", {"entities" : qUnion([Q0]), "endBoundEntityBody" : qUnion([Q1]), "depth" : 681 * mm, "hasSecondDirection" : true, "secondDirectionOppositeDirection" : true, "secondDirectionDepth" : 79 * mm});
        }
        {
            var Q0;
            Q0=qCreatedBy(makeId("Top.planeOp"),FACE);
            var sketch = newSketch(context, id + "F30", { "sketchPlane" : qUnion([Q0])});
            skLineSegment(sketch, "E100", {"start": v(281, -42.5) * mm, "end": v(281, -81.5) * mm});
            skLineSegment(sketch, "E101", {"start": v(289, -89.5) * mm, "end": v(333, -89.5) * mm});
            skLineSegment(sketch, "E102", {"start": v(341, -81.5) * mm, "end": v(341, 50.5) * mm});
            skPoint(sketch, "E103.visualSharp", {"position": v(281, -89.5) * mm});
            skArc(sketch, "E103.filletArc", {"start": v(281, -81.5) * mm, "mid": v(283.34, -87.16) * mm, "end": v(289, -89.5) * mm});
            skPoint(sketch, "E104.visualSharp", {"position": v(341, -89.5) * mm});
            skArc(sketch, "E104.filletArc", {"start": v(333, -89.5) * mm, "mid": v(338.66, -87.16) * mm, "end": v(341, -81.5) * mm});
            skLineSegment(sketch, "E105.0", {"start": v(335, -81.5) * mm, "end": v(335, 50.5) * mm});
            skLineSegment(sketch, "E105.1", {"start": v(287, -42.5) * mm, "end": v(287, -81.5) * mm});
            skArc(sketch, "E105.2", {"start": v(287, -81.5) * mm, "mid": v(287.59, -82.91) * mm, "end": v(289, -83.5) * mm});
            skLineSegment(sketch, "E105.3", {"start": v(289, -83.5) * mm, "end": v(333, -83.5) * mm});
            skArc(sketch, "E105.4", {"start": v(333, -83.5) * mm, "mid": v(334.41, -82.91) * mm, "end": v(335, -81.5) * mm});
            skLineSegment(sketch, "E106", {"start": v(281, -42.5) * mm, "end": v(287, -42.5) * mm});
            skLineSegment(sketch, "E107", {"start": v(335, 50.5) * mm, "end": v(341, 50.5) * mm});
            skSolve(sketch);
        }
        {
            var Q0;
            Q0=qSketchRegion(id+"F30",true);
            extrude(context, id + "F31", {"entities" : qUnion([Q0]), "depth" : 90 * mm});
        }
        {
            var Q0;
            Q0=makeQuery(id+"F31.opExtrude","SWEPT_BODY",BODY,{"disambiguationData":[OSD([sQuery(id+"F30.wireOp",EDGE,"E100"),sQuery(id+"F30.wireOp",EDGE,"E101"),sQuery(id+"F30.wireOp",EDGE,"E102"),sQuery(id+"F30.wireOp",EDGE,"E103.filletArc"),sQuery(id+"F30.wireOp",EDGE,"E104.filletArc"),sQuery(id+"F30.wireOp",EDGE,"E105.0"),sQuery(id+"F30.wireOp",EDGE,"E105.1"),sQuery(id+"F30.wireOp",EDGE,"E105.2"),sQuery(id+"F30.wireOp",EDGE,"E105.3"),sQuery(id+"F30.wireOp",EDGE,"E105.4"),sQuery(id+"F30.wireOp",EDGE,"E106"),sQuery(id+"F30.wireOp",EDGE,"E107")])]});
            transform(context, id + "F32", {"entities" : qUnion([Q0]), "transformType" : TransformType.TRANSLATION_3D, "dx" : 0 * mm, "dy" : 0 * mm, "dz" : 10 * mm, "makeCopy" : false});
        }
        {
            var Q0;
            Q0=makeQuery(id+"F31.opExtrude","SWEPT_FACE",FACE,{"disambiguationData":[OSD([sQuery(id+"F30.wireOp",EDGE,"E102")])]});
            var sketch = newSketch(context, id + "F33", { "sketchPlane" : qUnion([Q0])});
            skLineSegment(sketch, "E108.bottom", {"start": v(-50.5, 80) * mm, "end": v(29.5, 80) * mm, "construction": true});
            skLineSegment(sketch, "E108.top", {"start": v(-50.5, 30) * mm, "end": v(29.5, 30) * mm, "construction": true});
            skLineSegment(sketch, "E108.left", {"start": v(-50.5, 80) * mm, "end": v(-50.5, 30) * mm, "construction": true});
            skLineSegment(sketch, "E108.right", {"start": v(29.5, 80) * mm, "end": v(29.5, 30) * mm, "construction": true});
            skLineSegment(sketch, "E109", {"start": v(-81.5, 55) * mm, "end": v(50.5, 55) * mm, "construction": true});
            skCircle(sketch, "E110", {"center": v(-50.5, 80) * mm, "radius": 5.5 * mm});
            skCircle(sketch, "E111", {"center": v(29.5, 80) * mm, "radius": 5.5 * mm});
            skCircle(sketch, "E112", {"center": v(-50.5, 30) * mm, "radius": 5.5 * mm});
            skCircle(sketch, "E113", {"center": v(29.5, 30) * mm, "radius": 5.5 * mm});
            skSolve(sketch);
        }
        {
            var Q0;
            Q0=qSketchRegion(id+"F33",true);
            extrude(context, id + "F34", {"entities" : qUnion([Q0]), "operationType" : NewBodyOperationType.REMOVE, "endBound" : BoundingType.UP_TO_NEXT, "oppositeDirection" : true, "depth" : 25 * mm});
        }
        {
            var Q0;
            Q0=makeQuery(id+"F31.opExtrude","SWEPT_FACE",FACE,{"disambiguationData":[OSD([sQuery(id+"F30.wireOp",EDGE,"E100")])]});
            var sketch = newSketch(context, id + "F35", { "sketchPlane" : qUnion([Q0])});
            skLineSegment(sketch, "E114", {"start": v(81.5, 55) * mm, "end": v(42.5, 55) * mm, "construction": true});
            skCircle(sketch, "E115", {"center": v(59.5, 80) * mm, "radius": 5.5 * mm});
            skCircle(sketch, "E116", {"center": v(59.5, 30) * mm, "radius": 5.5 * mm});
            skSolve(sketch);
        }
        {
            var Q0;
            Q0=qSketchRegion(id+"F35",true);
            extrude(context, id + "F36", {"entities" : qUnion([Q0]), "operationType" : NewBodyOperationType.REMOVE, "endBound" : BoundingType.UP_TO_NEXT, "oppositeDirection" : true, "depth" : 25 * mm, "hasSecondDirection" : true, "secondDirectionBound" : SecondDirectionBoundingType.THROUGH_ALL, "secondDirectionOppositeDirection" : false, "secondDirectionDepth" : 25 * mm});
        }
        {
            var Q0;
            Q0=makeQuery(id+"F31.opExtrude","SWEPT_FACE",FACE,{"disambiguationData":[OSD([sQuery(id+"F30.wireOp",EDGE,"E101")])]});
            var sketch = newSketch(context, id + "F37", { "sketchPlane" : qUnion([Q0])});
            skLineSegment(sketch, "E117", {"start": v(311, 100) * mm, "end": v(311, 10) * mm, "construction": true});
            skLineSegment(sketch, "E118", {"start": v(333, 55) * mm, "end": v(289, 55) * mm, "construction": true});
            skCircle(sketch, "E119", {"center": v(311, 90) * mm, "radius": 4.4 * mm});
            skCircle(sketch, "E120", {"center": v(311, 20) * mm, "radius": 4.4 * mm});
            skSolve(sketch);
        }
        {
            var Q0;
            Q0=qSketchRegion(id+"F37",true);
            extrude(context, id + "F38", {"entities" : qUnion([Q0]), "operationType" : NewBodyOperationType.REMOVE, "endBound" : BoundingType.UP_TO_NEXT, "oppositeDirection" : true, "depth" : 25 * mm});
        }
        {
            var Q0;
            Q0=makeQuery(id+"F22.opPattern","COPY",FACE,{"derivedFrom":makeQuery(id+"F21.opExtrude","CAP_FACE",FACE,{"disambiguationData":[OSD([sQuery(id+"F20.wireOp",EDGE,"E52"),sQuery(id+"F20.wireOp",EDGE,"E53"),sQuery(id+"F20.wireOp",EDGE,"E54"),sQuery(id+"F20.wireOp",EDGE,"E55"),sQuery(id+"F20.wireOp",EDGE,"E56"),sQuery(id+"F20.wireOp",EDGE,"E57"),sQuery(id+"F20.wireOp",EDGE,"E58"),sQuery(id+"F20.wireOp",EDGE,"E59"),sQuery(id+"F20.wireOp",EDGE,"E60"),sQuery(id+"F20.wireOp",EDGE,"E61"),sQuery(id+"F20.wireOp",EDGE,"E62"),sQuery(id+"F20.wireOp",EDGE,"E63"),sQuery(id+"F20.wireOp",EDGE,"E64"),sQuery(id+"F20.wireOp",EDGE,"E65"),sQuery(id+"F20.wireOp",EDGE,"E66"),sQuery(id+"F20.wireOp",EDGE,"E67"),sQuery(id+"F20.wireOp",EDGE,"E68"),sQuery(id+"F20.wireOp",EDGE,"E69"),sQuery(id+"F20.wireOp",EDGE,"E70.filletArc"),sQuery(id+"F20.wireOp",EDGE,"E71.filletArc"),sQuery(id+"F20.wireOp",EDGE,"E72"),sQuery(id+"F20.wireOp",EDGE,"E73"),sQuery(id+"F20.wireOp",EDGE,"E75"),sQuery(id+"F20.wireOp",EDGE,"E77"),sQuery(id+"F20.wireOp",EDGE,"E78")])],"isStart":true}),"instanceName":"1"});
            var sketch = newSketch(context, id + "F39", { "sketchPlane" : qUnion([Q0])});
            skCircle(sketch, "E121", {"center": v(-89.5, -20) * mm, "radius": 10 * mm});
            skCircle(sketch, "E122", {"center": v(-89.5, -20) * mm, "radius": 5 * mm});
            skSolve(sketch);
        }
        {
            var Q0;
            Q0=qSketchRegion(id+"F39",true);
            extrude(context, id + "F40", {"entities" : qUnion([Q0]), "depth" : 13 * mm});
        }
        {
            var Q0;
            Q0=makeQuery(id+"F40.opExtrude","SWEPT_BODY",BODY,{"disambiguationData":[OSD([sQuery(id+"F39.wireOp",EDGE,"E121"),sQuery(id+"F39.wireOp",EDGE,"E122")])]});
            transform(context, id + "F41", {"entities" : qUnion([Q0]), "transformType" : TransformType.TRANSLATION_3D, "dx" : 625 * mm, "dy" : 0 * mm, "dz" : 0 * mm, "makeCopy" : true});
        }
        {
            var Q0;
            Q0=qCreatedBy(makeId("Front.planeOp"),FACE);
            var sketch = newSketch(context, id + "F42", { "sketchPlane" : qUnion([Q0])});
            skLineSegment(sketch, "E123", {"start": v(-56.83, 135.42) * mm, "end": v(-20.46, 135.42) * mm, "construction": true});
            skLineSegment(sketch, "E124", {"start": v(-52.91, 135.42) * mm, "end": v(-52.91, 140.98) * mm});
            skLineSegment(sketch, "E125", {"start": v(-52.91, 140.98) * mm, "end": v(-27.91, 140.98) * mm});
            skLineSegment(sketch, "E126", {"start": v(-27.91, 140.98) * mm, "end": v(-27.91, 145.67) * mm});
            skLineSegment(sketch, "E127", {"start": v(-27.91, 145.67) * mm, "end": v(-25.41, 145.67) * mm});
            skLineSegment(sketch, "E128", {"start": v(-25.41, 145.67) * mm, "end": v(-25.41, 135.42) * mm});
            skLineSegment(sketch, "E129", {"start": v(-25.41, 135.42) * mm, "end": v(-52.91, 135.42) * mm});
            skSolve(sketch);
        }
        {
            var Q0;
            Q0=qSketchRegion(id+"F42",true);
            var Q1;
            Q1=sQuery(id+"F42.wireOp",EDGE,"E123");
            revolve(context, id + "F43", {"entities" : qUnion([Q0]), "axis" : qUnion([Q1]), "revolveType" : RevolveType.FULL});
        }
        {
            var Q0;
            Q0=makeQuery(id+"F43.opRevolve","SWEPT_FACE",FACE,{"disambiguationData":[OSD([sQuery(id+"F42.wireOp",EDGE,"E128")])]});
            var sketch = newSketch(context, id + "F44", { "sketchPlane" : qUnion([Q0])});
            skCircle(sketch, "E130.cCircle", {"center": v(0, 135.42) * mm, "radius": 7.5 * mm, "construction": true});
            skLineSegment(sketch, "E130.0", {"start": v(8.66, 135.16) * mm, "end": v(4.1, 127.8) * mm});
            skLineSegment(sketch, "E130.1", {"start": v(4.1, 127.8) * mm, "end": v(-4.55, 128.06) * mm});
            skLineSegment(sketch, "E130.2", {"start": v(-4.55, 128.06) * mm, "end": v(-8.66, 135.68) * mm});
            skLineSegment(sketch, "E130.3", {"start": v(-8.66, 135.68) * mm, "end": v(-4.1, 143.05) * mm});
            skLineSegment(sketch, "E130.4", {"start": v(-4.1, 143.05) * mm, "end": v(4.55, 142.8) * mm});
            skLineSegment(sketch, "E130.5", {"start": v(4.55, 142.8) * mm, "end": v(8.66, 135.16) * mm});
            skPoint(sketch, "E130.0.midPoint", {"position": v(6.38, 131.48) * mm});
            skSolve(sketch);
        }
        {
            var Q0;
            Q0=qSketchRegion(id+"F44",true);
            var Q1;
            Q1=makeQuery(id+"F44.imprint","IMPRINT",FACE,{"disambiguationData":[TD([[makeQuery(id+"F44.imprint","IMPRINT",EDGE,{"derivedFrom":sQuery(id+"F44.wireOp",EDGE,"E130.0")}),-1.0]])]});
            extrude(context, id + "F45", {"entities" : qUnion([Q0, Q1]), "operationType" : NewBodyOperationType.ADD, "depth" : 6.5 * mm});
        }
        {
            var Q0;
            Q0=makeQuery(id+"F43.opRevolve","SWEPT_EDGE",EDGE,{"disambiguationData":[OSD([sQuery(id+"F42.wireOp",EDGE,"E124"),sQuery(id+"F42.wireOp",EDGE,"E125")])]});
            var Q1;
            Q1=makeQuery(id+"F43.opRevolve","SWEPT_EDGE",EDGE,{"disambiguationData":[OSD([sQuery(id+"F42.wireOp",EDGE,"E127"),sQuery(id+"F42.wireOp",EDGE,"E128")])]});
            chamfer(context, id + "F46", {"entities" : qUnion([Q0, Q1]), "width" : 1 * mm, "tangentPropagation" : true});
        }
        {
            var Q0;
            Q0=makeQuery(id+"F31.opExtrude","CAP_FACE",FACE,{"disambiguationData":[OSD([sQuery(id+"F30.wireOp",EDGE,"E100"),sQuery(id+"F30.wireOp",EDGE,"E101"),sQuery(id+"F30.wireOp",EDGE,"E102"),sQuery(id+"F30.wireOp",EDGE,"E103.filletArc"),sQuery(id+"F30.wireOp",EDGE,"E104.filletArc"),sQuery(id+"F30.wireOp",EDGE,"E105.0"),sQuery(id+"F30.wireOp",EDGE,"E105.1"),sQuery(id+"F30.wireOp",EDGE,"E105.2"),sQuery(id+"F30.wireOp",EDGE,"E105.3"),sQuery(id+"F30.wireOp",EDGE,"E105.4"),sQuery(id+"F30.wireOp",EDGE,"E106"),sQuery(id+"F30.wireOp",EDGE,"E107")])],"isStart":false});
            var sketch = newSketch(context, id + "F47", { "sketchPlane" : qUnion([Q0])});
            skLineSegment(sketch, "E131.0", {"start": v(281, -74.5) * mm, "end": v(275, -74.5) * mm, "construction": true});
            skLineSegment(sketch, "E132", {"start": v(339, -3.29) * mm, "end": v(339, -39.91) * mm});
            skLineSegment(sketch, "E133", {"start": v(339, -39.91) * mm, "end": v(283, -79.12) * mm});
            skLineSegment(sketch, "E134", {"start": v(283, -79.12) * mm, "end": v(283, -42.5) * mm});
            skLineSegment(sketch, "E135", {"start": v(283, -42.5) * mm, "end": v(339, -3.29) * mm});
            skLineSegment(sketch, "E136", {"start": v(311, -89.5) * mm, "end": v(311, 37.52) * mm, "construction": true});
            skSolve(sketch);
        }
        {
            var Q0;
            Q0=makeQuery(id+"F31.opExtrude","CAP_FACE",FACE,{"disambiguationData":[OSD([sQuery(id+"F30.wireOp",EDGE,"E100"),sQuery(id+"F30.wireOp",EDGE,"E101"),sQuery(id+"F30.wireOp",EDGE,"E102"),sQuery(id+"F30.wireOp",EDGE,"E103.filletArc"),sQuery(id+"F30.wireOp",EDGE,"E104.filletArc"),sQuery(id+"F30.wireOp",EDGE,"E105.0"),sQuery(id+"F30.wireOp",EDGE,"E105.1"),sQuery(id+"F30.wireOp",EDGE,"E105.2"),sQuery(id+"F30.wireOp",EDGE,"E105.3"),sQuery(id+"F30.wireOp",EDGE,"E105.4"),sQuery(id+"F30.wireOp",EDGE,"E106"),sQuery(id+"F30.wireOp",EDGE,"E107")])],"isStart":false});
            var Q1;
            Q1=makeQuery(id+"F31.opExtrude","CAP_FACE",FACE,{"disambiguationData":[OSD([sQuery(id+"F30.wireOp",EDGE,"E100"),sQuery(id+"F30.wireOp",EDGE,"E101"),sQuery(id+"F30.wireOp",EDGE,"E102"),sQuery(id+"F30.wireOp",EDGE,"E103.filletArc"),sQuery(id+"F30.wireOp",EDGE,"E104.filletArc"),sQuery(id+"F30.wireOp",EDGE,"E105.0"),sQuery(id+"F30.wireOp",EDGE,"E105.1"),sQuery(id+"F30.wireOp",EDGE,"E105.2"),sQuery(id+"F30.wireOp",EDGE,"E105.3"),sQuery(id+"F30.wireOp",EDGE,"E105.4"),sQuery(id+"F30.wireOp",EDGE,"E106"),sQuery(id+"F30.wireOp",EDGE,"E107")])],"isStart":true});
            cPlane(context, id + "F48", {"entities" : qUnion([Q0, Q1]), "cplaneType" : CPlaneType.MID_PLANE, "offset" : 150 * mm, "width" : 150 * mm, "height" : 150 * mm});
        }
        {
            var Q0;
            Q0=makeQuery(id+"F1.opExtrude","SWEPT_EDGE",EDGE,{"disambiguationData":[OSD([sQuery(id+"F0.wireOp",EDGE,"E2"),sQuery(id+"F0.wireOp",EDGE,"E5")])]});
            cPlane(context, id + "F49", {"entities" : qUnion([Q0]), "cplaneType" : CPlaneType.MID_PLANE, "offset" : 150 * mm, "width" : 150 * mm, "height" : 150 * mm});
        }
        {
            var Q0;
            Q0=makeQuery(id+"F31.opExtrude","SWEPT_BODY",BODY,{"disambiguationData":[OSD([sQuery(id+"F30.wireOp",EDGE,"E100"),sQuery(id+"F30.wireOp",EDGE,"E101"),sQuery(id+"F30.wireOp",EDGE,"E102"),sQuery(id+"F30.wireOp",EDGE,"E103.filletArc"),sQuery(id+"F30.wireOp",EDGE,"E104.filletArc"),sQuery(id+"F30.wireOp",EDGE,"E105.0"),sQuery(id+"F30.wireOp",EDGE,"E105.1"),sQuery(id+"F30.wireOp",EDGE,"E105.2"),sQuery(id+"F30.wireOp",EDGE,"E105.3"),sQuery(id+"F30.wireOp",EDGE,"E105.4"),sQuery(id+"F30.wireOp",EDGE,"E106"),sQuery(id+"F30.wireOp",EDGE,"E107")])]});
            var Q1;
            Q1=qCreatedBy(id+"F49.planeOp",FACE);
            mirror(context, id + "F50", {"entities" : qUnion([Q0]), "mirrorPlane" : qUnion([Q1])});
        }
        {
            var Q0;
            Q0=makeQuery(id+"F1.opExtrude","SWEPT_FACE",FACE,{"disambiguationData":[OSD([sQuery(id+"F0.wireOp",EDGE,"E1")])]});
            var sketch = newSketch(context, id + "F51", { "sketchPlane" : qUnion([Q0])});
            skCircle(sketch, "E137.cCircle", {"center": v(-127, 31.5) * mm, "radius": 8.5 * mm, "construction": true});
            skLineSegment(sketch, "E137.0", {"start": v(-135.5, 26.6) * mm, "end": v(-135.5, 36.4) * mm});
            skLineSegment(sketch, "E137.1", {"start": v(-135.5, 36.4) * mm, "end": v(-127, 41.31) * mm});
            skLineSegment(sketch, "E137.2", {"start": v(-127, 41.31) * mm, "end": v(-118.5, 36.4) * mm});
            skLineSegment(sketch, "E137.3", {"start": v(-118.5, 36.4) * mm, "end": v(-118.5, 26.6) * mm});
            skLineSegment(sketch, "E137.4", {"start": v(-118.5, 26.6) * mm, "end": v(-127, 21.69) * mm});
            skLineSegment(sketch, "E137.5", {"start": v(-127, 21.69) * mm, "end": v(-135.5, 26.6) * mm});
            skPoint(sketch, "E137.0.midPoint", {"position": v(-135.5, 31.5) * mm});
            skCircle(sketch, "E138", {"center": v(-127, 31.5) * mm, "radius": 4.25 * mm});
            skSolve(sketch);
        }
        {
            var Q0;
            Q0=qSketchRegion(id+"F51",true);
            extrude(context, id + "F52", {"entities" : qUnion([Q0]), "depth" : 7 * mm});
        }
        {
            var Q0;
            Q0=makeQuery(id+"F1.opExtrude","SWEPT_FACE",FACE,{"disambiguationData":[OSD([sQuery(id+"F0.wireOp",EDGE,"E1")])]});
            var sketch = newSketch(context, id + "F53", { "sketchPlane" : qUnion([Q0])});
            skCircle(sketch, "E139", {"center": v(-139.7, 50.1) * mm, "radius": 5.4 * mm});
            skCircle(sketch, "E140.cCircle", {"center": v(-139.7, 50.1) * mm, "radius": 9.5 * mm, "construction": true});
            skLineSegment(sketch, "E140.0", {"start": v(-149.2, 44.62) * mm, "end": v(-149.2, 55.58) * mm});
            skLineSegment(sketch, "E140.1", {"start": v(-149.2, 55.58) * mm, "end": v(-139.7, 61.07) * mm});
            skLineSegment(sketch, "E140.2", {"start": v(-139.7, 61.07) * mm, "end": v(-130.2, 55.58) * mm});
            skLineSegment(sketch, "E140.3", {"start": v(-130.2, 55.58) * mm, "end": v(-130.2, 44.62) * mm});
            skLineSegment(sketch, "E140.4", {"start": v(-130.2, 44.62) * mm, "end": v(-139.7, 39.13) * mm});
            skLineSegment(sketch, "E140.5", {"start": v(-139.7, 39.13) * mm, "end": v(-149.2, 44.62) * mm});
            skPoint(sketch, "E140.0.midPoint", {"position": v(-149.2, 50.1) * mm});
            skSolve(sketch);
        }
        {
            var Q0;
            Q0=qSketchRegion(id+"F53",true);
            extrude(context, id + "F54", {"entities" : qUnion([Q0]), "depth" : 7 * mm});
        }
        {
            var Q0;
            Q0=makeQuery(id+"F1.opExtrude","SWEPT_FACE",FACE,{"disambiguationData":[OSD([sQuery(id+"F0.wireOp",EDGE,"E3.0")])]});
            var sketch = newSketch(context, id + "F55", { "sketchPlane" : qUnion([Q0])});
            skLineSegment(sketch, "E141", {"start": v(-127.5, 44.85) * mm, "end": v(127.5, 44.85) * mm, "construction": true});
            skLineSegment(sketch, "E142", {"start": v(-107, 75.85) * mm, "end": v(-148.5, 61.25) * mm});
            skCircle(sketch, "E143", {"center": v(-127.5, 44.85) * mm, "radius": 6.65 * mm});
            skLineSegment(sketch, "E144.MirrorCS", {"start": v(107, 75.85) * mm, "end": v(148.5, 61.25) * mm});
            skCircle(sketch, "E145.MirrorC", {"center": v(127.5, 44.85) * mm, "radius": 6.65 * mm});
            skLineSegment(sketch, "E146.MirrorCS", {"start": v(-107, 13.85) * mm, "end": v(-148.5, 28.45) * mm});
            skLineSegment(sketch, "E147.MirrorCS", {"start": v(107, 13.85) * mm, "end": v(148.5, 28.45) * mm});
            skLineSegment(sketch, "E148", {"start": v(-107, 75.85) * mm, "end": v(107, 75.85) * mm});
            skLineSegment(sketch, "E149", {"start": v(-107, 13.85) * mm, "end": v(107, 13.85) * mm});
            skCircle(sketch, "E150", {"center": v(-87.9, 44.85) * mm, "radius": 12.1 * mm});
            skCircle(sketch, "E151.MirrorC", {"center": v(87.9, 44.85) * mm, "radius": 12.1 * mm});
            skLineSegment(sketch, "E152", {"start": v(-87.9, 56.95) * mm, "end": v(87.9, 56.95) * mm});
            skLineSegment(sketch, "E153.MirrorCS", {"start": v(-87.9, 32.75) * mm, "end": v(87.9, 32.75) * mm});
            skLineSegment(sketch, "E154", {"start": v(-148.5, 61.25) * mm, "end": v(-148.5, 28.45) * mm});
            skLineSegment(sketch, "E155", {"start": v(148.5, 61.25) * mm, "end": v(148.5, 28.45) * mm});
            skSolve(sketch);
        }
        {
            var Q0;
            Q0=qSketchRegion(id+"F55",true);
            extrude(context, id + "F56", {"entities" : qUnion([Q0]), "depth" : 18 * mm});
        }
        {
            var Q0;
            Q0=makeQuery(id+"F56.opExtrude","CAP_FACE",FACE,{"disambiguationData":[OSD([sQuery(id+"F55.wireOp",EDGE,"1EFQZ6ap-uAg3-N8OW-0aFA-wIDavsOpqr7z"),sQuery(id+"F55.wireOp",EDGE,"E142"),sQuery(id+"F55.wireOp",EDGE,"E143"),sQuery(id+"F55.wireOp",EDGE,"E144.MirrorCS"),sQuery(id+"F55.wireOp",EDGE,"E145.MirrorC"),sQuery(id+"F55.wireOp",EDGE,"dfcf7d93-0b25-4aa2-80d3-010f8d92ff410.MirrorC"),sQuery(id+"F55.wireOp",EDGE,"E146.MirrorCS"),sQuery(id+"F55.wireOp",EDGE,"E147.MirrorCS"),sQuery(id+"F55.wireOp",EDGE,"E148"),sQuery(id+"F55.wireOp",EDGE,"E149"),sQuery(id+"F55.wireOp",EDGE,"E150"),sQuery(id+"F55.wireOp",EDGE,"E151.MirrorC"),sQuery(id+"F55.wireOp",EDGE,"E152"),sQuery(id+"F55.wireOp",EDGE,"E153.MirrorCS")])],"isStart":false});
            var sketch = newSketch(context, id + "F57", { "sketchPlane" : qUnion([Q0])});
            skCircle(sketch, "E156", {"center": v(-127.5, 44.85) * mm, "radius": 12.6 * mm});
            skCircle(sketch, "E157", {"center": v(127.5, 44.85) * mm, "radius": 12.6 * mm});
            skSolve(sketch);
        }
        {
            var Q0;
            Q0=qSketchRegion(id+"F57",true);
            extrude(context, id + "F58", {"entities" : qUnion([Q0]), "operationType" : NewBodyOperationType.REMOVE, "oppositeDirection" : true, "depth" : 11.5 * mm});
        }
        {
            var Q0;
            Q0=makeQuery(id+"F56.opExtrude","CAP_EDGE",EDGE,{"disambiguationData":[OSD([sQuery(id+"F55.wireOp",EDGE,"E151.MirrorC")])],"isStart":false});
            var Q1;
            Q1=makeQuery(id+"F56.opExtrude","CAP_EDGE",EDGE,{"disambiguationData":[OSD([sQuery(id+"F55.wireOp",EDGE,"E153.MirrorCS")])],"isStart":true});
            fillet(context, id + "F59", {"entities" : qUnion([Q0, Q1]), "radius" : 7 * mm, "tangentPropagation" : true, "allowEdgeOverflow" : false});
        }
        {
            var Q0;
            Q0=makeQuery(id+"F56.opExtrude","SWEPT_EDGE",EDGE,{"disambiguationData":[OSD([sQuery(id+"F55.wireOp",EDGE,"E142"),sQuery(id+"F55.wireOp",EDGE,"E148")])]});
            var Q1;
            Q1=makeQuery(id+"F56.opExtrude","SWEPT_EDGE",EDGE,{"disambiguationData":[OSD([sQuery(id+"F55.wireOp",EDGE,"E144.MirrorCS"),sQuery(id+"F55.wireOp",EDGE,"E148")])]});
            var Q2;
            Q2=makeQuery(id+"F56.opExtrude","SWEPT_EDGE",EDGE,{"disambiguationData":[OSD([sQuery(id+"F55.wireOp",EDGE,"E146.MirrorCS"),sQuery(id+"F55.wireOp",EDGE,"E149")])]});
            var Q3;
            Q3=makeQuery(id+"F56.opExtrude","SWEPT_EDGE",EDGE,{"disambiguationData":[OSD([sQuery(id+"F55.wireOp",EDGE,"E147.MirrorCS"),sQuery(id+"F55.wireOp",EDGE,"E149")])]});
            var Q4;
            Q4=makeQuery(id+"F56.opExtrude","SWEPT_EDGE",EDGE,{"disambiguationData":[OSD([sQuery(id+"F55.wireOp",EDGE,"E142"),sQuery(id+"F55.wireOp",EDGE,"E154")])]});
            var Q5;
            Q5=makeQuery(id+"F56.opExtrude","SWEPT_EDGE",EDGE,{"disambiguationData":[OSD([sQuery(id+"F55.wireOp",EDGE,"E146.MirrorCS"),sQuery(id+"F55.wireOp",EDGE,"E154")])]});
            var Q6;
            Q6=makeQuery(id+"F56.opExtrude","SWEPT_EDGE",EDGE,{"disambiguationData":[OSD([sQuery(id+"F55.wireOp",EDGE,"E144.MirrorCS"),sQuery(id+"F55.wireOp",EDGE,"E155")])]});
            var Q7;
            Q7=makeQuery(id+"F56.opExtrude","SWEPT_EDGE",EDGE,{"disambiguationData":[OSD([sQuery(id+"F55.wireOp",EDGE,"E147.MirrorCS"),sQuery(id+"F55.wireOp",EDGE,"E155")])]});
            fillet(context, id + "F60", {"entities" : qUnion([Q0, Q1, Q2, Q3, Q4, Q5, Q6, Q7]), "radius" : 18 * mm, "tangentPropagation" : true, "allowEdgeOverflow" : false});
        }
        {
            var Q0;
            Q0=makeQuery(id+"F29.opExtrude","SWEPT_FACE",FACE,{"disambiguationData":[OSD([sQuery(id+"F28.wireOp",EDGE,"E99.right")])]});
            var sketch = newSketch(context, id + "F61", { "sketchPlane" : qUnion([Q0])});
            skLineSegment(sketch, "E158.bottom", {"start": v(354, -30) * mm, "end": v(364, -30) * mm});
            skLineSegment(sketch, "E158.top", {"start": v(354, -70) * mm, "end": v(364, -70) * mm});
            skLineSegment(sketch, "E158.left", {"start": v(354, -30) * mm, "end": v(354, -70) * mm});
            skLineSegment(sketch, "E158.right", {"start": v(364, -30) * mm, "end": v(364, -70) * mm});
            skSolve(sketch);
        }
        {
            var Q0;
            {var subQ4=sQuery(id+"F61.wireOp",EDGE,"E158.bottom");Q0=makeQuery(id+"F61.imprint","IMPRINT",FACE,{"disambiguationData":[TD([[makeQuery(id+"F61.imprint","IMPRINT",EDGE,{"derivedFrom":subQ4}),-1.0]])]});}
            extrude(context, id + "F62", {"entities" : qUnion([Q0]), "oppositeDirection" : true, "depth" : 10 * mm});
        }
        {
            var Q0;
            Q0=makeQuery(id+"F62.opExtrude","SWEPT_EDGE",EDGE,{"disambiguationData":[OSD([sQuery(id+"F61.wireOp",EDGE,"E158.top"),sQuery(id+"F61.wireOp",EDGE,"E158.right")])]});
            var Q1;
            Q1=makeQuery(id+"F62.opExtrude","CAP_EDGE",EDGE,{"disambiguationData":[OSD([sQuery(id+"F61.wireOp",EDGE,"E158.top")])],"isStart":true});
            var Q2;
            Q2=makeQuery(id+"F62.opExtrude","SWEPT_EDGE",EDGE,{"disambiguationData":[OSD([sQuery(id+"F61.wireOp",EDGE,"E158.top"),sQuery(id+"F61.wireOp",EDGE,"E158.left")])]});
            var Q3;
            Q3=makeQuery(id+"F62.opExtrude","CAP_EDGE",EDGE,{"disambiguationData":[OSD([sQuery(id+"F61.wireOp",EDGE,"E158.top")])],"isStart":false});
            chamfer(context, id + "F63", {"entities" : qUnion([Q0, Q1, Q2, Q3]), "width" : 2 * mm, "tangentPropagation" : true});
        }
        {
            var Q0;
            Q0=makeQuery(id+"F62.opExtrude","SWEPT_BODY",BODY,{"disambiguationData":[OSD([sQuery(id+"F61.wireOp",EDGE,"E158.bottom"),sQuery(id+"F61.wireOp",EDGE,"E158.top"),sQuery(id+"F61.wireOp",EDGE,"E158.left"),sQuery(id+"F61.wireOp",EDGE,"E158.right")])]});
            var Q1;
            Q1=qCreatedBy(id+"F49.planeOp",FACE);
            mirror(context, id + "F64", {"entities" : qUnion([Q0]), "mirrorPlane" : qUnion([Q1])});
        }
    });
